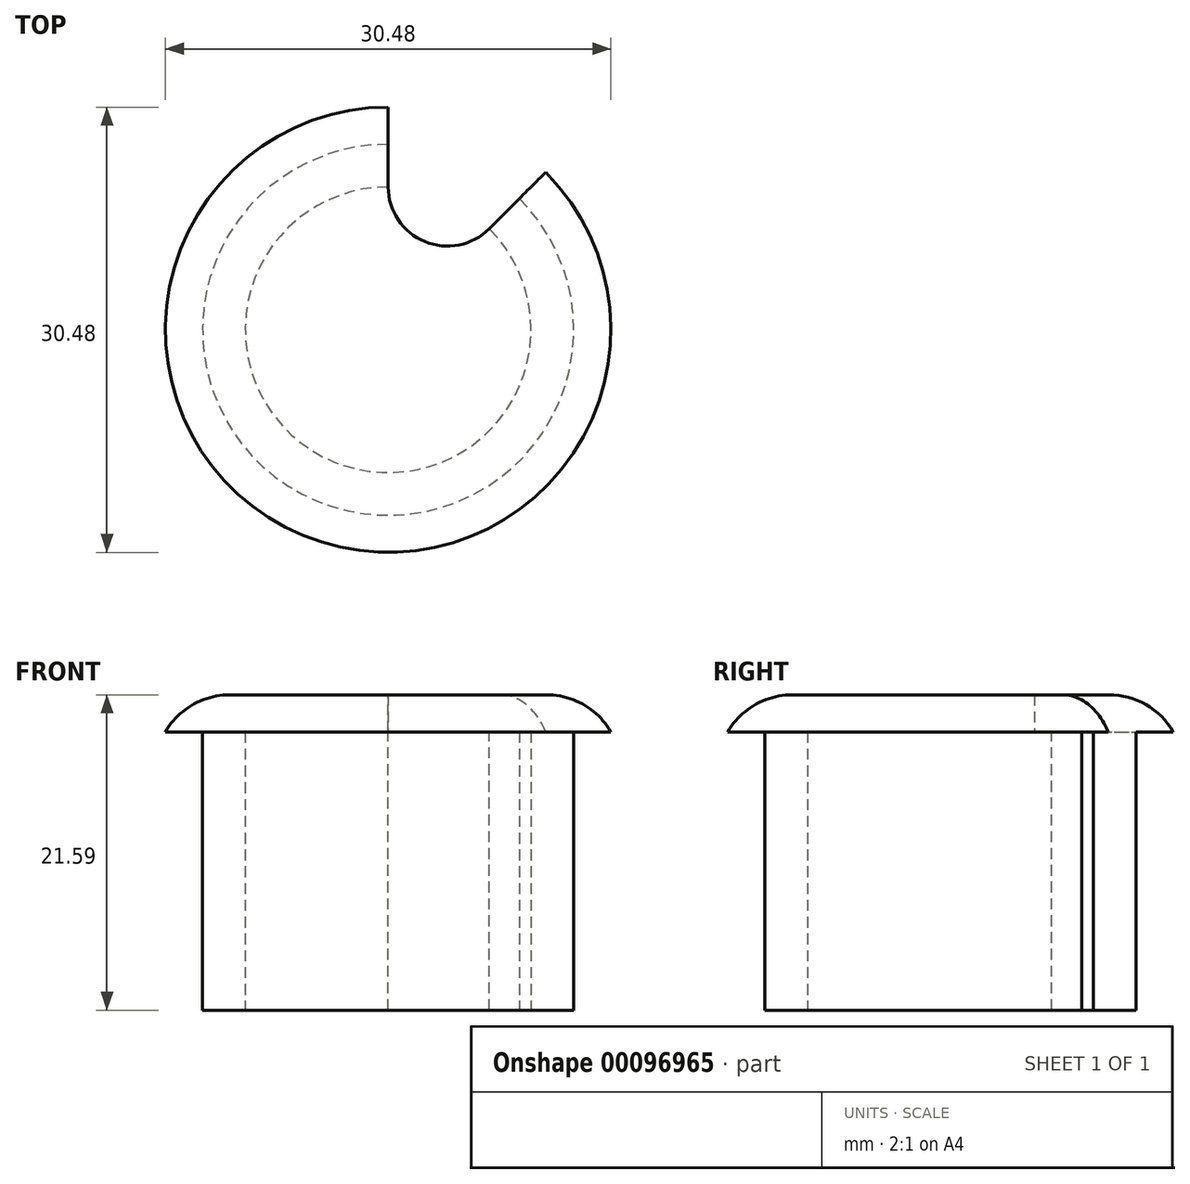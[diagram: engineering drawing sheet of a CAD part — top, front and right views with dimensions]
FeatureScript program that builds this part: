
annotation { "Feature Type Name" : "Feature", "Feature Type Description" : "" }
export const myFeature = defineFeature(function(context is Context, id is Id, definition is map)
    precondition{}
    {
        {
            var Q0;
            Q0=qCreatedBy(makeId("Right.planeOp"),FACE);
            var sketch = newSketch(context, id + "F0", { "sketchPlane" : qUnion([Q0])});
            skLineSegment(sketch, "E0", {"start": v(0, 21.59) * mm, "end": v(15.24, 21.59) * mm});
            skLineSegment(sketch, "E1", {"start": v(15.24, 21.59) * mm, "end": v(15.24, 19.05) * mm});
            skLineSegment(sketch, "E2", {"start": v(15.24, 19.05) * mm, "end": v(12.7, 19.05) * mm});
            skLineSegment(sketch, "E3", {"start": v(12.7, 19.05) * mm, "end": v(12.7, 0) * mm});
            skLineSegment(sketch, "E4", {"start": v(12.7, 0) * mm, "end": v(9.78, 0) * mm});
            skLineSegment(sketch, "E5", {"start": v(9.78, 0) * mm, "end": v(9.78, 19.05) * mm});
            skLineSegment(sketch, "E6", {"start": v(0, 19.05) * mm, "end": v(9.78, 19.05) * mm});
            skLineSegment(sketch, "E7", {"start": v(0, 21.59) * mm, "end": v(0, 19.05) * mm});
            skSolve(sketch);
        }
        {
            var Q0;
            Q0=makeQuery(id+"F0.imprint","IMPRINT",FACE,{"disambiguationData":[TD([[makeQuery(id+"F0.imprint","IMPRINT",EDGE,{"derivedFrom":sQuery(id+"F0.wireOp",EDGE,"E0")}),-1.0]])]});
            var Q1;
            Q1=sQuery(id+"F0.wireOp",EDGE,"E7");
            revolve(context, id + "F1", {"entities" : qUnion([Q0]), "axis" : qUnion([Q1]), "revolveType" : RevolveType.ONE_DIRECTION, "oppositeDirection" : true, "angle" : 315 * degree});
        }
        {
            var Q0;
            Q0=makeQuery(id+"F1.opRevolve","SWEPT_EDGE",EDGE,{"disambiguationData":[OSD([sQuery(id+"F0.wireOp",EDGE,"E0"),sQuery(id+"F0.wireOp",EDGE,"E1")])]});
            fillet(context, id + "F2", {"entities" : qUnion([Q0]), "radius" : 5.08 * mm, "tangentPropagation" : true, "allowEdgeOverflow" : false});
        }
        {
            var Q0;
            Q0=makeQuery(id+"F1.opRevolve","SWEPT_FACE",FACE,{"disambiguationData":[OSD([sQuery(id+"F0.wireOp",EDGE,"E6")])]});
            var sketch = newSketch(context, id + "F3", { "sketchPlane" : qUnion([Q0])});
            skArc(sketch, "E8", {"start": v(6.91, -6.91) * mm, "mid": v(2.5, -6.04) * mm, "end": v(0, -9.78) * mm});
            skSolve(sketch);
        }
        {
            var Q0;
            Q0=makeQuery(id+"F3.imprint","IMPRINT",FACE,{"disambiguationData":[TD([[makeQuery(id+"F3.imprint","IMPRINT",EDGE,{"derivedFrom":sQuery(id+"F3.wireOp",EDGE,"E8")}),-1.0]])]});
            extrude(context, id + "F4", {"entities" : qUnion([Q0]), "operationType" : NewBodyOperationType.ADD, "oppositeDirection" : true, "depth" : 2.54 * mm});
        }
    });
